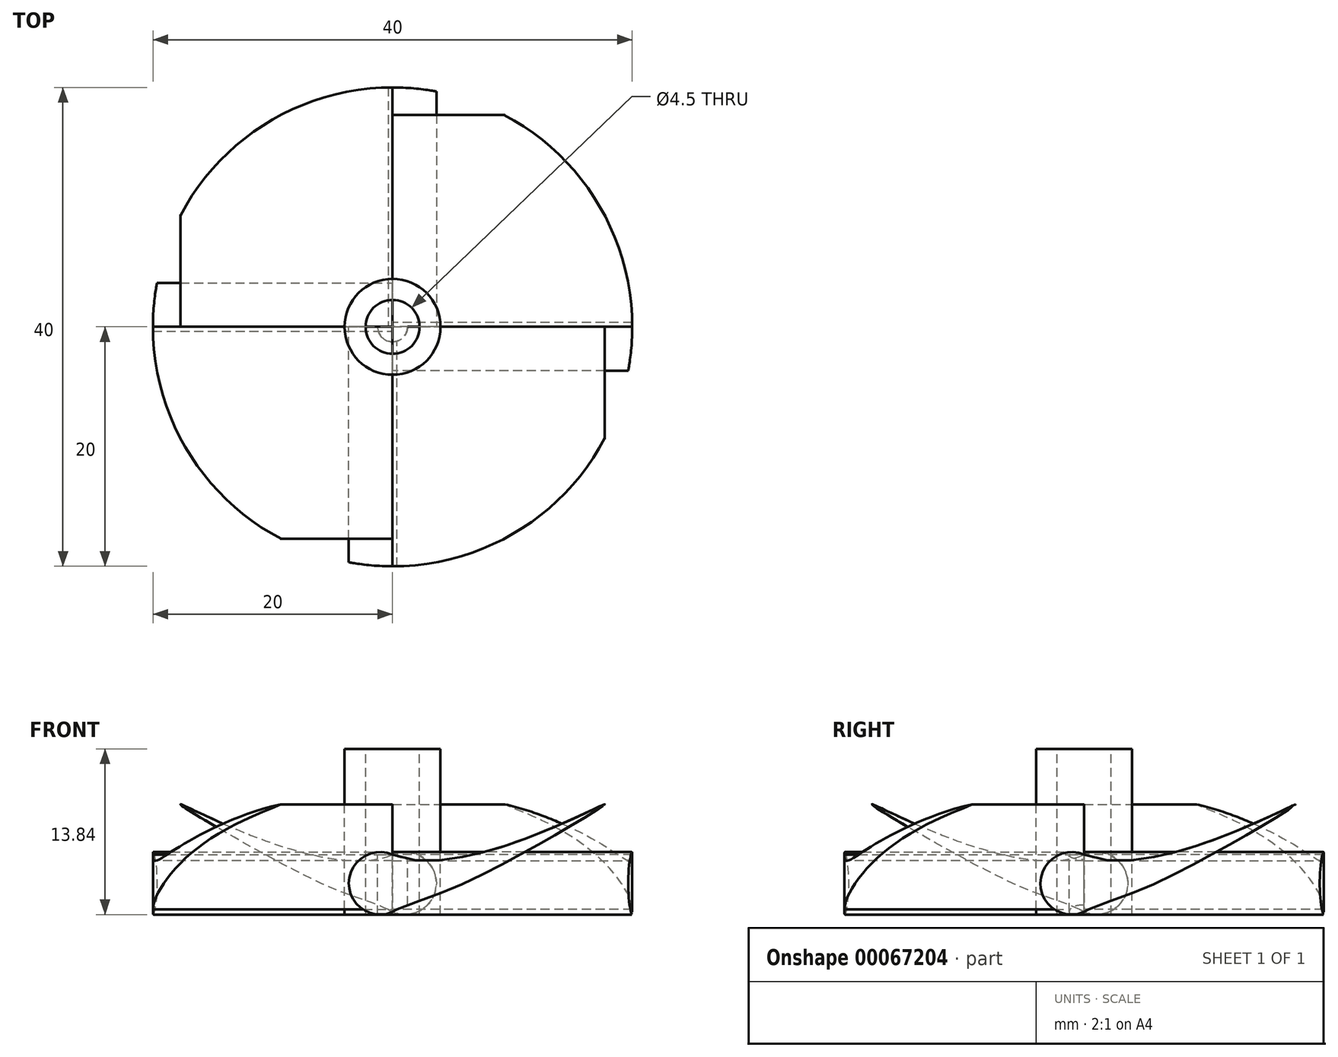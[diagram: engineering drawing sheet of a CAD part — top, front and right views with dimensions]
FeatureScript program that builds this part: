
annotation { "Feature Type Name" : "Feature", "Feature Type Description" : "" }
export const myFeature = defineFeature(function(context is Context, id is Id, definition is map)
    precondition{}
    {
        {
            var Q0;
            Q0=qCreatedBy(makeId("Top.planeOp"),FACE);
            var sketch = newSketch(context, id + "F0", { "sketchPlane" : qUnion([Q0])});
            skCircle(sketch, "E0", {"center": v(0, 0) * mm, "radius": 4 * mm});
            skLineSegment(sketch, "E1", {"start": v(0, 0) * mm, "end": v(7.96, 7.96) * mm, "construction": true});
            skLineSegment(sketch, "E2", {"start": v(0, 0) * mm, "end": v(-13.16, -13.16) * mm, "construction": true});
            skLineSegment(sketch, "E3", {"start": v(0, 0) * mm, "end": v(30.75, 0) * mm, "construction": true});
            skCircle(sketch, "E4", {"center": v(0, 0) * mm, "radius": 20 * mm});
            skCircle(sketch, "E5", {"center": v(0, 0) * mm, "radius": 51.75 * mm});
            skCircle(sketch, "E6", {"center": v(0, 0) * mm, "radius": 2.25 * mm});
            skSolve(sketch);
        }
        {
            var Q0;
            Q0=makeQuery(id+"F0.imprint","IMPRINT",FACE,{"disambiguationData":[TD([[makeQuery(id+"F0.imprint","IMPRINT",EDGE,{"derivedFrom":sQuery(id+"F0.wireOp",EDGE,"E0")}),1.0]])]});
            extrude(context, id + "F1", {"entities" : qUnion([Q0]), "oppositeDirection" : true, "depth" : 5 * mm, "hasSecondDirection" : true, "secondDirectionOppositeDirection" : false, "secondDirectionDepth" : 8.84 * mm});
        }
        {
            var Q0;
            Q0=qCreatedBy(makeId("Front.planeOp"),FACE);
            var sketch = newSketch(context, id + "F2", { "sketchPlane" : qUnion([Q0])});
            skCircle(sketch, "E7", {"center": v(-1.05, -2.4) * mm, "radius": 2.6 * mm});
            skPoint(sketch, "E7.first.point", {"position": v(0, 0) * mm});
            skPoint(sketch, "E7.second.point", {"position": v(0, -4.78) * mm});
            skPoint(sketch, "E7.third.point", {"position": v(-2.1, 0) * mm});
            skFitSpline(sketch, "E8", {"points": [v(0, -4.78) * mm, v(5.95, -2.4) * mm, v(17.7, 4.21) * mm, v(0, 0) * mm], "startDerivative": vector(17.54, 10.12) * mm, "endDerivative": vector(-40.36, 17.13) * mm});
            skSolve(sketch);
        }
        {
            var Q0;
            Q0 = qSketchRegion(id + "F2", true);
            extrude(context, id + "F3", {"entities" : qUnion([Q0]), "depth" : 25 * mm});
        }
        {
            var Q0;
            Q0=makeQuery(id+"F3.opExtrude","SWEPT_BODY",BODY,{"disambiguationData":[OSD([sQuery(id+"F2.wireOp",EDGE,"E7"),sQuery(id+"F2.wireOp",EDGE,"E8")])]});
            var Q1;
            Q1=makeQuery(id+"F1.opExtrude","SWEPT_FACE",FACE,{"disambiguationData":[OSD([sQuery(id+"F0.wireOp",EDGE,"E0")])]});
            transform(context, id + "F4", {"entities" : qUnion([Q0]), "transformType" : TransformType.ROTATION, "transformAxis" : qUnion([Q1]), "angle" : 180 * degree, "makeCopy" : true});
        }
        {
            var Q0;
            Q0=makeQuery(id+"F3.opExtrude","SWEPT_BODY",BODY,{"disambiguationData":[OSD([sQuery(id+"F2.wireOp",EDGE,"E7"),sQuery(id+"F2.wireOp",EDGE,"E8")])]});
            var Q1;
            Q1=makeQuery(id+"F1.opExtrude","SWEPT_FACE",FACE,{"disambiguationData":[OSD([sQuery(id+"F0.wireOp",EDGE,"E0")])]});
            transform(context, id + "F5", {"entities" : qUnion([Q0]), "transformType" : TransformType.ROTATION, "transformAxis" : qUnion([Q1]), "angle" : 90 * degree, "makeCopy" : true});
        }
        {
            var Q0;
            Q0=makeQuery(id+"F5.opPattern","COPY",BODY,{"derivedFrom":makeQuery(id+"F3.opExtrude","SWEPT_BODY",BODY,{"disambiguationData":[OSD([sQuery(id+"F2.wireOp",EDGE,"E7"),sQuery(id+"F2.wireOp",EDGE,"E8")])]}),"instanceName":"1"});
            var Q1;
            Q1=makeQuery(id+"F1.opExtrude","SWEPT_FACE",FACE,{"disambiguationData":[OSD([sQuery(id+"F0.wireOp",EDGE,"E0")])]});
            transform(context, id + "F6", {"entities" : qUnion([Q0]), "transformType" : TransformType.ROTATION, "transformAxis" : qUnion([Q1]), "angle" : 180 * degree, "makeCopy" : true});
        }
        {
            var Q0;
            Q0=makeQuery(id+"F0.imprint","IMPRINT",FACE,{"disambiguationData":[TD([[makeQuery(id+"F0.imprint","IMPRINT",EDGE,{"derivedFrom":sQuery(id+"F0.wireOp",EDGE,"E4")}),-1.0]])]});
            extrude(context, id + "F7", {"entities" : qUnion([Q0]), "operationType" : NewBodyOperationType.REMOVE, "oppositeDirection" : true, "depth" : 25 * mm, "hasSecondDirection" : true, "secondDirectionOppositeDirection" : false, "secondDirectionDepth" : 25 * mm});
        }
        {
            var Q0;
            Q0=sQuery(id+"F0.wireOp",VERTEX,"E1.start");
            var Q1;
            Q1=makeQuery(id+"F3.opExtrude","SWEPT_BODY",BODY,{"disambiguationData":[OSD([sQuery(id+"F2.wireOp",EDGE,"E7"),sQuery(id+"F2.wireOp",EDGE,"E8")])]});
            hole(context, id + "F8", {"style" : HoleStyle.SIMPLE, "holeDiameter" : 2.5 * mm, "endStyle" : HoleEndStyle.THROUGH, "locations" : qUnion([Q0]), "scope" : qUnion([Q1])});
        }
    });
